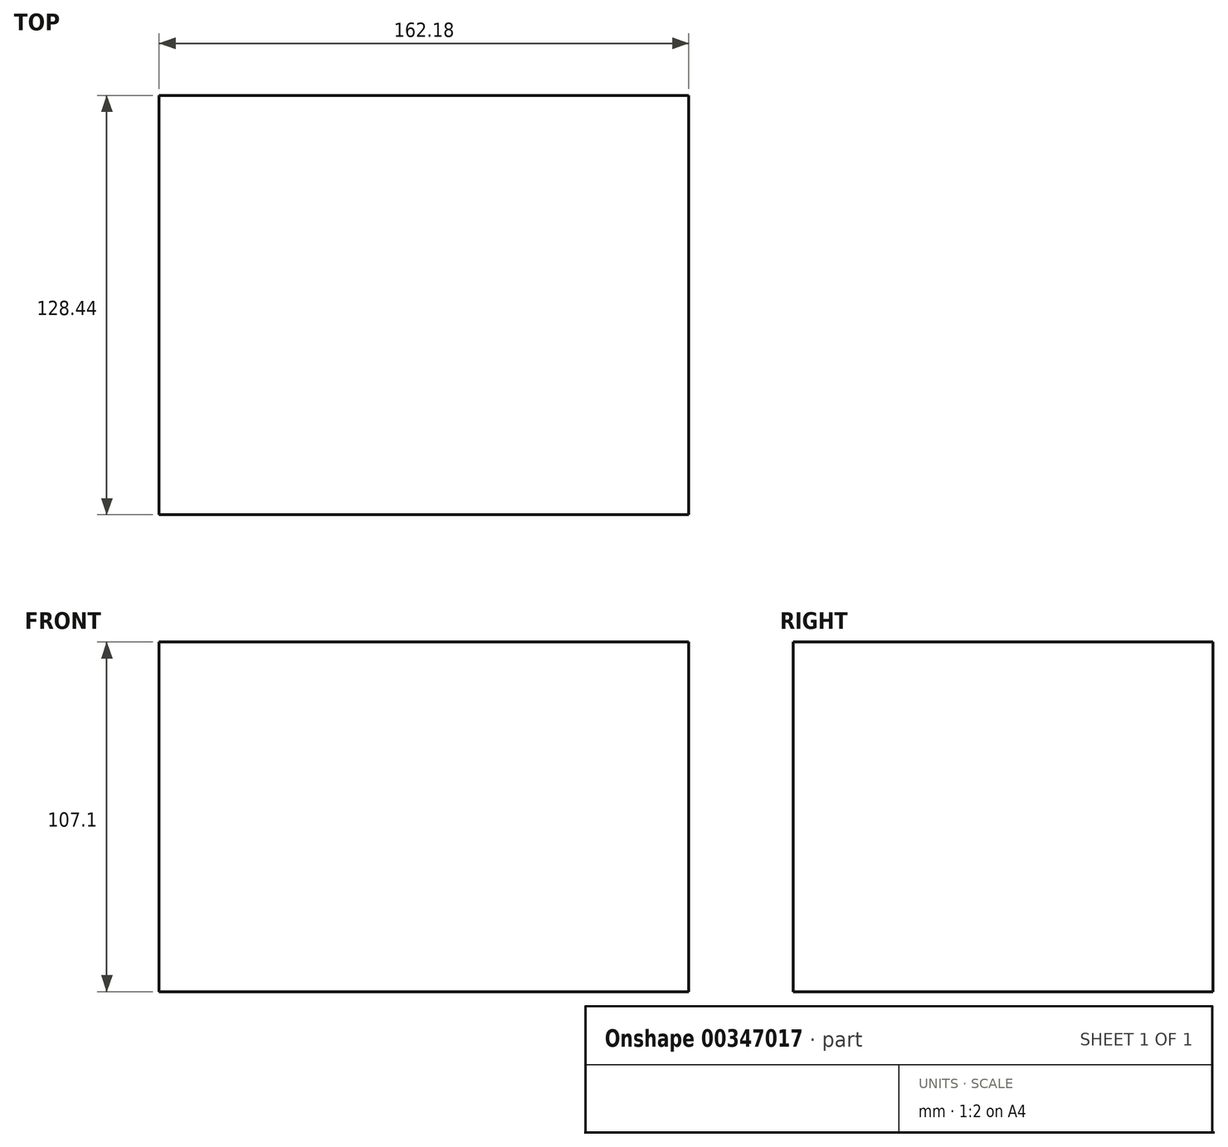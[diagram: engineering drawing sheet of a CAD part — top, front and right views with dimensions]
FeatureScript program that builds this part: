
annotation { "Feature Type Name" : "Feature", "Feature Type Description" : "" }
export const myFeature = defineFeature(function(context is Context, id is Id, definition is map)
    precondition{}
    {
        {
            var Q0;
            Q0=qCreatedBy(makeId("Right.planeOp"),FACE);
            var sketch = newSketch(context, id + "F0", { "sketchPlane" : qUnion([Q0])});
            skLineSegment(sketch, "E0.bottom", {"start": v(-76.63, 67.19) * mm, "end": v(51.81, 67.19) * mm});
            skLineSegment(sketch, "E0.top", {"start": v(-76.63, -39.91) * mm, "end": v(51.81, -39.91) * mm});
            skLineSegment(sketch, "E0.left", {"start": v(-76.63, 67.19) * mm, "end": v(-76.63, -39.91) * mm});
            skLineSegment(sketch, "E0.right", {"start": v(51.81, 67.19) * mm, "end": v(51.81, -39.91) * mm});
            skSolve(sketch);
        }
        {
            var Q0;
            Q0 = qSketchRegion(id + "F0", true);
            extrude(context, id + "F1", {"entities" : qUnion([Q0]), "depth" : 162.18 * mm});
        }
    });
